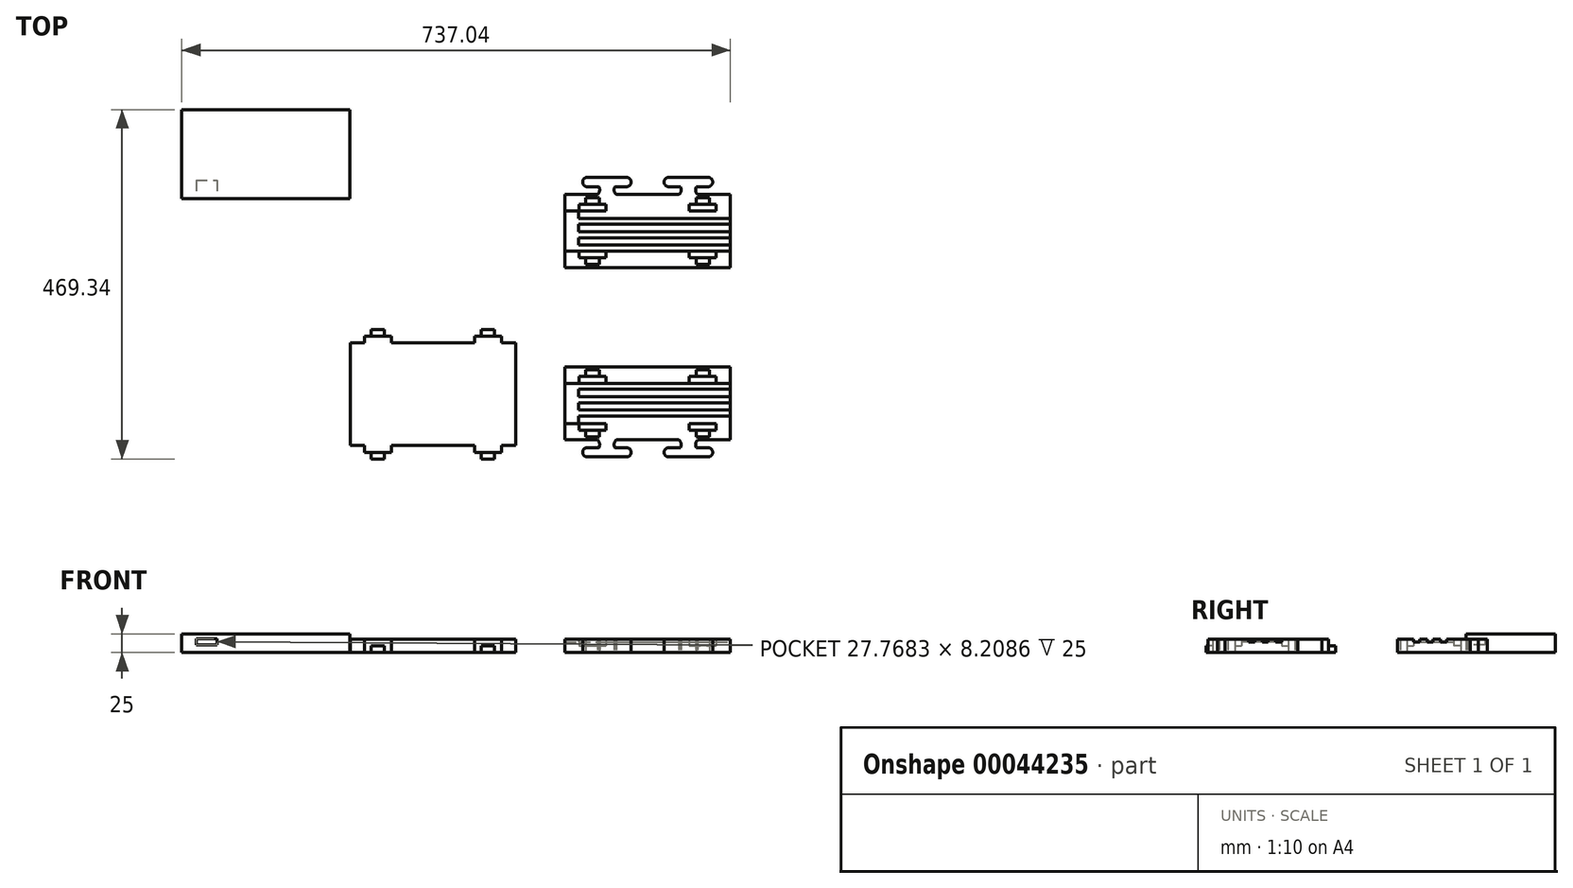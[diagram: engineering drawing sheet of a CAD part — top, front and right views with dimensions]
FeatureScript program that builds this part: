
annotation { "Feature Type Name" : "Feature", "Feature Type Description" : "" }
export const myFeature = defineFeature(function(context is Context, id is Id, definition is map)
    precondition{}
    {
        {
            var Q0;
            Q0=qCreatedBy(makeId("Top.planeOp"),FACE);
            var sketch = newSketch(context, id + "F0", { "sketchPlane" : qUnion([Q0])});
            skLineSegment(sketch, "E0.left", {"start": v(28.08, 92) * mm, "end": v(28.08, -2) * mm});
            skLineSegment(sketch, "E0.right", {"start": v(250.08, 92) * mm, "end": v(250.08, -2) * mm});
            skPoint(sketch, "E1", {"position": v(28.08, 72) * mm});
            skPoint(sketch, "E2", {"position": v(28.08, 18) * mm});
            skPoint(sketch, "E3", {"position": v(28.08, 64) * mm});
            skPoint(sketch, "E4", {"position": v(28.08, 28) * mm});
            skPoint(sketch, "E5", {"position": v(28.08, 54) * mm});
            skPoint(sketch, "E6", {"position": v(29.26, 46) * mm});
            skPoint(sketch, "E7", {"position": v(28.08, 36) * mm});
            skLineSegment(sketch, "E8", {"start": v(28.08, 72) * mm, "end": v(250.08, 72) * mm});
            skLineSegment(sketch, "E9", {"start": v(28.08, 54) * mm, "end": v(250.08, 54) * mm});
            skLineSegment(sketch, "E10", {"start": v(28.08, 36) * mm, "end": v(250.08, 36) * mm});
            skLineSegment(sketch, "E11", {"start": v(28.08, 18) * mm, "end": v(250.08, 18) * mm});
            skPoint(sketch, "E12", {"position": v(102.08, 92) * mm});
            skPoint(sketch, "E13", {"position": v(176.08, 92) * mm});
            skLineSegment(sketch, "E14", {"start": v(102.08, 92) * mm, "end": v(102.08, -2) * mm, "construction": true});
            skLineSegment(sketch, "E15", {"start": v(176.08, 92) * mm, "end": v(176.08, -2) * mm, "construction": true});
            skPoint(sketch, "E16", {"position": v(46.08, 72) * mm});
            skLineSegment(sketch, "E17", {"start": v(46.08, 72) * mm, "end": v(46.08, 18) * mm, "construction": true});
            skPoint(sketch, "E18", {"position": v(46.08, 64) * mm});
            skPoint(sketch, "E19", {"position": v(46.08, 46) * mm});
            skPoint(sketch, "E20", {"position": v(46.08, 28) * mm});
            skLineSegment(sketch, "E21", {"start": v(46.08, 46) * mm, "end": v(250.08, 46) * mm});
            skLineSegment(sketch, "E22", {"start": v(46.08, 64) * mm, "end": v(250.08, 64) * mm});
            skLineSegment(sketch, "E23", {"start": v(46.08, 28) * mm, "end": v(250.08, 28) * mm});
            skPoint(sketch, "E24", {"position": v(213.08, 92) * mm});
            skPoint(sketch, "E25", {"position": v(65.08, 92) * mm});
            skLineSegment(sketch, "E26", {"start": v(65.08, 92) * mm, "end": v(65.08, -2) * mm, "construction": true});
            skLineSegment(sketch, "E27", {"start": v(213.08, 92) * mm, "end": v(213.08, -2) * mm, "construction": true});
            skLineSegment(sketch, "E28", {"start": v(46.08, 64) * mm, "end": v(46.08, 54) * mm});
            skLineSegment(sketch, "E29", {"start": v(46.08, 46) * mm, "end": v(46.08, 36) * mm});
            skLineSegment(sketch, "E30", {"start": v(46.08, 28) * mm, "end": v(46.08, 18) * mm});
            skPoint(sketch, "E31", {"position": v(139.08, 92) * mm});
            skLineSegment(sketch, "E32", {"start": v(139.08, 92) * mm, "end": v(139.08, -2) * mm, "construction": true});
            skLineSegment(sketch, "E33", {"start": v(193.85, -2) * mm, "end": v(193.85, -27) * mm, "construction": true});
            skLineSegment(sketch, "E34", {"start": v(84.31, -2) * mm, "end": v(84.31, -27) * mm, "construction": true});
            skLineSegment(sketch, "E35", {"start": v(84.31, -14.5) * mm, "end": v(193.85, -14.5) * mm, "construction": true});
            skLineSegment(sketch, "E36", {"start": v(84.31, -14.5) * mm, "end": v(31.64, -14.5) * mm, "construction": true});
            skLineSegment(sketch, "E37", {"start": v(193.85, -14.5) * mm, "end": v(246.52, -14.5) * mm, "construction": true});
            skArc(sketch, "E38", {"start": v(206.54, -4) * mm, "mid": v(203.7, -8.9) * mm, "end": v(204.52, -14.5) * mm});
            skArc(sketch, "E39.MirrorCS", {"start": v(97, -4) * mm, "mid": v(94.16, -8.9) * mm, "end": v(94.99, -14.5) * mm});
            skArc(sketch, "E40.MirrorCS", {"start": v(71.63, -4) * mm, "mid": v(74.47, -8.9) * mm, "end": v(73.64, -14.5) * mm});
            skLineSegment(sketch, "E41", {"start": v(73.64, -14.5) * mm, "end": v(57.98, -14.5) * mm});
            skLineSegment(sketch, "E42", {"start": v(94.99, -14.5) * mm, "end": v(110.65, -14.5) * mm});
            skLineSegment(sketch, "E43", {"start": v(183.17, -14.5) * mm, "end": v(167.51, -14.5) * mm});
            skLineSegment(sketch, "E44", {"start": v(204.52, -14.5) * mm, "end": v(220.18, -14.5) * mm});
            skArc(sketch, "E45", {"start": v(57.98, -14.5) * mm, "mid": v(51.73, -20.75) * mm, "end": v(57.98, -27) * mm});
            skArc(sketch, "E46.MirrorCS", {"start": v(110.65, -14.5) * mm, "mid": v(116.9, -20.75) * mm, "end": v(110.65, -27) * mm});
            skArc(sketch, "E47.MirrorCS", {"start": v(167.51, -14.5) * mm, "mid": v(161.26, -20.75) * mm, "end": v(167.51, -27) * mm});
            skArc(sketch, "E48.MirrorCS", {"start": v(220.18, -14.5) * mm, "mid": v(226.43, -20.75) * mm, "end": v(220.18, -27) * mm});
            skLineSegment(sketch, "E49", {"start": v(57.98, -27) * mm, "end": v(110.65, -27) * mm});
            skLineSegment(sketch, "E50", {"start": v(167.51, -27) * mm, "end": v(220.18, -27) * mm});
            skLineSegment(sketch, "E51", {"start": v(-11.33, 160.77) * mm, "end": v(328.55, 160.77) * mm});
            skLineSegment(sketch, "E52.MirrorCS", {"start": v(176.57, 323.54) * mm, "end": v(176.08, 323.54) * mm});
            skPoint(sketch, "E53", {"position": v(65.08, 18) * mm});
            skPoint(sketch, "E54", {"position": v(83.08, 18) * mm});
            skPoint(sketch, "E55", {"position": v(47.08, 18) * mm});
            skPoint(sketch, "E56", {"position": v(65.08, 9) * mm});
            skPoint(sketch, "E57", {"position": v(65.08, 0) * mm});
            skLineSegment(sketch, "E58", {"start": v(47.08, 18) * mm, "end": v(47.08, 9) * mm});
            skLineSegment(sketch, "E59", {"start": v(47.08, 9) * mm, "end": v(65.08, 9) * mm});
            skLineSegment(sketch, "E60", {"start": v(65.08, 9) * mm, "end": v(83.08, 9) * mm});
            skLineSegment(sketch, "E61", {"start": v(83.08, 9) * mm, "end": v(83.08, 18) * mm});
            skLineSegment(sketch, "E62", {"start": v(65.08, 0) * mm, "end": v(74.08, 0) * mm});
            skLineSegment(sketch, "E63", {"start": v(65.08, 0) * mm, "end": v(56.08, 0) * mm});
            skLineSegment(sketch, "E64", {"start": v(74.08, 0) * mm, "end": v(74.08, 9) * mm});
            skLineSegment(sketch, "E65", {"start": v(56.08, 0) * mm, "end": v(56.08, 9) * mm});
            skLineSegment(sketch, "E66.MirrorCS", {"start": v(195.08, 9) * mm, "end": v(195.08, 18) * mm});
            skLineSegment(sketch, "E67.MirrorCS", {"start": v(213.08, 9) * mm, "end": v(195.08, 9) * mm});
            skLineSegment(sketch, "E68.MirrorCS", {"start": v(231.08, 9) * mm, "end": v(213.08, 9) * mm});
            skLineSegment(sketch, "E69.MirrorCS", {"start": v(231.08, 18) * mm, "end": v(231.08, 9) * mm});
            skLineSegment(sketch, "E70.MirrorCS", {"start": v(204.08, 0) * mm, "end": v(204.08, 9) * mm});
            skLineSegment(sketch, "E71.MirrorCS", {"start": v(213.08, 0) * mm, "end": v(204.08, 0) * mm});
            skLineSegment(sketch, "E72.MirrorCS", {"start": v(213.08, 0) * mm, "end": v(222.08, 0) * mm});
            skLineSegment(sketch, "E73.MirrorCS", {"start": v(222.08, 0) * mm, "end": v(222.08, 9) * mm});
            skPoint(sketch, "E74", {"position": v(250.08, 45) * mm});
            skLineSegment(sketch, "E75", {"start": v(250.08, 45) * mm, "end": v(290.41, 45) * mm, "construction": true});
            skLineSegment(sketch, "E76.MirrorCS", {"start": v(195.08, 81) * mm, "end": v(195.08, 72) * mm});
            skLineSegment(sketch, "E77.MirrorCS", {"start": v(231.08, 72) * mm, "end": v(231.08, 81) * mm});
            skLineSegment(sketch, "E78.MirrorCS", {"start": v(231.08, 81) * mm, "end": v(213.08, 81) * mm});
            skLineSegment(sketch, "E79.MirrorCS", {"start": v(213.08, 81) * mm, "end": v(195.08, 81) * mm});
            skLineSegment(sketch, "E80.MirrorCS", {"start": v(204.08, 90) * mm, "end": v(204.08, 81) * mm});
            skLineSegment(sketch, "E81.MirrorCS", {"start": v(213.08, 90) * mm, "end": v(204.08, 90) * mm});
            skLineSegment(sketch, "E82.MirrorCS", {"start": v(213.08, 90) * mm, "end": v(222.08, 90) * mm});
            skLineSegment(sketch, "E83.MirrorCS", {"start": v(222.08, 90) * mm, "end": v(222.08, 81) * mm});
            skLineSegment(sketch, "E84.MirrorCS", {"start": v(83.08, 81) * mm, "end": v(83.08, 72) * mm});
            skLineSegment(sketch, "E85.MirrorCS", {"start": v(65.08, 81) * mm, "end": v(83.08, 81) * mm});
            skLineSegment(sketch, "E86.MirrorCS", {"start": v(47.08, 81) * mm, "end": v(65.08, 81) * mm});
            skLineSegment(sketch, "E87.MirrorCS", {"start": v(47.08, 72) * mm, "end": v(47.08, 81) * mm});
            skLineSegment(sketch, "E88.MirrorCS", {"start": v(56.08, 90) * mm, "end": v(56.08, 81) * mm});
            skLineSegment(sketch, "E89.MirrorCS", {"start": v(65.08, 90) * mm, "end": v(56.08, 90) * mm});
            skLineSegment(sketch, "E90.MirrorCS", {"start": v(65.08, 90) * mm, "end": v(74.08, 90) * mm});
            skLineSegment(sketch, "E91.MirrorCS", {"start": v(74.08, 90) * mm, "end": v(74.08, 81) * mm});
            skLineSegment(sketch, "E92", {"start": v(28.08, 92) * mm, "end": v(28.08, 94) * mm});
            skLineSegment(sketch, "E93", {"start": v(28.08, 94) * mm, "end": v(250.08, 94) * mm});
            skLineSegment(sketch, "E94", {"start": v(250.08, 94) * mm, "end": v(250.08, 92) * mm});
            skLineSegment(sketch, "E95", {"start": v(28.08, -2) * mm, "end": v(28.08, -4) * mm});
            skLineSegment(sketch, "E96", {"start": v(28.08, -4) * mm, "end": v(71.63, -4) * mm});
            skLineSegment(sketch, "E97", {"start": v(97, -4) * mm, "end": v(181.16, -4) * mm});
            skLineSegment(sketch, "E98", {"start": v(206.54, -4) * mm, "end": v(250.08, -4) * mm});
            skLineSegment(sketch, "E99", {"start": v(250.08, -4) * mm, "end": v(250.08, -2) * mm});
            skPoint(sketch, "E100.trimOffspring.start.orphan", {"position": v(211.13, -2) * mm});
            skArc(sketch, "E101.trimOffspring", {"start": v(181.16, -4) * mm, "mid": v(184, -8.9) * mm, "end": v(183.17, -14.5) * mm});
            skPoint(sketch, "E102.MirrorCS.start.orphan", {"position": v(174.62, -2) * mm});
            skPoint(sketch, "E103.start.orphan", {"position": v(176.57, -2) * mm});
            skPoint(sketch, "E104.orphan", {"position": v(158.31, -2) * mm});
            skPoint(sketch, "E105.orphan", {"position": v(119.85, -2) * mm});
            skPoint(sketch, "E106.start.orphan", {"position": v(103.55, -2) * mm});
            skPoint(sketch, "E107.orphan", {"position": v(65.08, -2) * mm});
            skPoint(sketch, "E108.orphan", {"position": v(67.03, -2) * mm});
            skLineSegment(sketch, "E109.MirrorCS", {"start": v(28.08, 227.54) * mm, "end": v(250.08, 227.54) * mm});
            skLineSegment(sketch, "E110.MirrorCS", {"start": v(74.08, 231.54) * mm, "end": v(74.08, 240.54) * mm});
            skLineSegment(sketch, "E111.MirrorCS", {"start": v(65.08, 231.54) * mm, "end": v(74.08, 231.54) * mm});
            skLineSegment(sketch, "E112.MirrorCS", {"start": v(65.08, 231.54) * mm, "end": v(56.08, 231.54) * mm});
            skLineSegment(sketch, "E113.MirrorCS", {"start": v(56.08, 231.54) * mm, "end": v(56.08, 240.54) * mm});
            skLineSegment(sketch, "E114.MirrorCS", {"start": v(65.08, 240.54) * mm, "end": v(83.08, 240.54) * mm});
            skLineSegment(sketch, "E115.MirrorCS", {"start": v(47.08, 240.54) * mm, "end": v(65.08, 240.54) * mm});
            skLineSegment(sketch, "E116.MirrorCS", {"start": v(83.08, 240.54) * mm, "end": v(83.08, 249.54) * mm});
            skLineSegment(sketch, "E117.MirrorCS", {"start": v(47.08, 249.54) * mm, "end": v(47.08, 240.54) * mm});
            skLineSegment(sketch, "E118.MirrorCS", {"start": v(28.08, 249.54) * mm, "end": v(250.08, 249.54) * mm});
            skLineSegment(sketch, "E119.MirrorCS", {"start": v(222.08, 231.54) * mm, "end": v(222.08, 240.54) * mm});
            skLineSegment(sketch, "E120.MirrorCS", {"start": v(213.08, 231.54) * mm, "end": v(222.08, 231.54) * mm});
            skLineSegment(sketch, "E121.MirrorCS", {"start": v(213.08, 231.54) * mm, "end": v(204.08, 231.54) * mm});
            skLineSegment(sketch, "E122.MirrorCS", {"start": v(204.08, 231.54) * mm, "end": v(204.08, 240.54) * mm});
            skLineSegment(sketch, "E123.MirrorCS", {"start": v(213.08, 240.54) * mm, "end": v(195.08, 240.54) * mm});
            skLineSegment(sketch, "E124.MirrorCS", {"start": v(231.08, 240.54) * mm, "end": v(213.08, 240.54) * mm});
            skLineSegment(sketch, "E125.MirrorCS", {"start": v(231.08, 249.54) * mm, "end": v(231.08, 240.54) * mm});
            skLineSegment(sketch, "E126.MirrorCS", {"start": v(195.08, 240.54) * mm, "end": v(195.08, 249.54) * mm});
            skLineSegment(sketch, "E127.MirrorCS", {"start": v(46.08, 257.54) * mm, "end": v(250.08, 257.54) * mm});
            skLineSegment(sketch, "E128.MirrorCS", {"start": v(28.08, 267.54) * mm, "end": v(250.08, 267.54) * mm});
            skLineSegment(sketch, "E129.MirrorCS", {"start": v(46.08, 275.54) * mm, "end": v(250.08, 275.54) * mm});
            skLineSegment(sketch, "E130.MirrorCS", {"start": v(28.08, 285.54) * mm, "end": v(250.08, 285.54) * mm});
            skLineSegment(sketch, "E131.MirrorCS", {"start": v(46.08, 293.54) * mm, "end": v(250.08, 293.54) * mm});
            skLineSegment(sketch, "E132.MirrorCS", {"start": v(28.08, 303.54) * mm, "end": v(250.08, 303.54) * mm});
            skLineSegment(sketch, "E133.MirrorCS", {"start": v(250.08, 229.54) * mm, "end": v(250.08, 323.54) * mm});
            skLineSegment(sketch, "E134.MirrorCS", {"start": v(250.08, 227.54) * mm, "end": v(250.08, 229.54) * mm});
            skLineSegment(sketch, "E135.MirrorCS", {"start": v(28.08, 229.54) * mm, "end": v(28.08, 227.54) * mm});
            skLineSegment(sketch, "E136.MirrorCS", {"start": v(28.08, 229.54) * mm, "end": v(28.08, 323.54) * mm});
            skLineSegment(sketch, "E137.MirrorCS", {"start": v(28.08, 323.54) * mm, "end": v(28.08, 325.54) * mm});
            skLineSegment(sketch, "E138.MirrorCS", {"start": v(250.08, 325.54) * mm, "end": v(250.08, 323.54) * mm});
            skLineSegment(sketch, "E139.MirrorCS", {"start": v(206.54, 325.54) * mm, "end": v(250.08, 325.54) * mm});
            skArc(sketch, "E140.MirrorCS", {"start": v(206.54, 325.54) * mm, "mid": v(203.7, 330.44) * mm, "end": v(204.52, 336.04) * mm});
            skLineSegment(sketch, "E141.MirrorCS", {"start": v(204.52, 336.04) * mm, "end": v(220.18, 336.04) * mm});
            skArc(sketch, "E142.MirrorCS", {"start": v(220.18, 336.04) * mm, "mid": v(226.43, 342.29) * mm, "end": v(220.18, 348.54) * mm});
            skLineSegment(sketch, "E143.MirrorCS", {"start": v(167.51, 348.54) * mm, "end": v(220.18, 348.54) * mm});
            skArc(sketch, "E144.MirrorCS", {"start": v(167.51, 336.04) * mm, "mid": v(161.26, 342.29) * mm, "end": v(167.51, 348.54) * mm});
            skLineSegment(sketch, "E145.MirrorCS", {"start": v(183.17, 336.04) * mm, "end": v(167.51, 336.04) * mm});
            skArc(sketch, "E146.MirrorCS", {"start": v(181.16, 325.54) * mm, "mid": v(184, 330.44) * mm, "end": v(183.17, 336.04) * mm});
            skLineSegment(sketch, "E147.MirrorCS", {"start": v(97, 325.54) * mm, "end": v(181.16, 325.54) * mm});
            skArc(sketch, "E148.MirrorCS", {"start": v(97, 325.54) * mm, "mid": v(94.16, 330.44) * mm, "end": v(94.99, 336.04) * mm});
            skLineSegment(sketch, "E149.MirrorCS", {"start": v(94.99, 336.04) * mm, "end": v(110.65, 336.04) * mm});
            skArc(sketch, "E150.MirrorCS", {"start": v(110.65, 336.04) * mm, "mid": v(116.9, 342.29) * mm, "end": v(110.65, 348.54) * mm});
            skLineSegment(sketch, "E151.MirrorCS", {"start": v(57.98, 348.54) * mm, "end": v(110.65, 348.54) * mm});
            skArc(sketch, "E152.MirrorCS", {"start": v(57.98, 336.04) * mm, "mid": v(51.73, 342.29) * mm, "end": v(57.98, 348.54) * mm});
            skLineSegment(sketch, "E153.MirrorCS", {"start": v(73.64, 336.04) * mm, "end": v(57.98, 336.04) * mm});
            skArc(sketch, "E154.MirrorCS", {"start": v(71.63, 325.54) * mm, "mid": v(74.47, 330.44) * mm, "end": v(73.64, 336.04) * mm});
            skLineSegment(sketch, "E155.MirrorCS", {"start": v(28.08, 325.54) * mm, "end": v(71.63, 325.54) * mm});
            skLineSegment(sketch, "E156.MirrorCS", {"start": v(83.08, 312.54) * mm, "end": v(83.08, 303.54) * mm});
            skLineSegment(sketch, "E157.MirrorCS", {"start": v(65.08, 312.54) * mm, "end": v(83.08, 312.54) * mm});
            skLineSegment(sketch, "E158.MirrorCS", {"start": v(47.08, 312.54) * mm, "end": v(65.08, 312.54) * mm});
            skLineSegment(sketch, "E159.MirrorCS", {"start": v(47.08, 303.54) * mm, "end": v(47.08, 312.54) * mm});
            skLineSegment(sketch, "E160.MirrorCS", {"start": v(56.08, 321.54) * mm, "end": v(56.08, 312.54) * mm});
            skLineSegment(sketch, "E161.MirrorCS", {"start": v(65.08, 321.54) * mm, "end": v(56.08, 321.54) * mm});
            skLineSegment(sketch, "E162.MirrorCS", {"start": v(65.08, 321.54) * mm, "end": v(74.08, 321.54) * mm});
            skLineSegment(sketch, "E163.MirrorCS", {"start": v(74.08, 321.54) * mm, "end": v(74.08, 312.54) * mm});
            skLineSegment(sketch, "E164.MirrorCS", {"start": v(195.08, 312.54) * mm, "end": v(195.08, 303.54) * mm});
            skLineSegment(sketch, "E165.MirrorCS", {"start": v(213.08, 312.54) * mm, "end": v(195.08, 312.54) * mm});
            skLineSegment(sketch, "E166.MirrorCS", {"start": v(231.08, 312.54) * mm, "end": v(213.08, 312.54) * mm});
            skLineSegment(sketch, "E167.MirrorCS", {"start": v(231.08, 303.54) * mm, "end": v(231.08, 312.54) * mm});
            skLineSegment(sketch, "E168.MirrorCS", {"start": v(222.08, 321.54) * mm, "end": v(222.08, 312.54) * mm});
            skLineSegment(sketch, "E169.MirrorCS", {"start": v(213.08, 321.54) * mm, "end": v(222.08, 321.54) * mm});
            skLineSegment(sketch, "E170.MirrorCS", {"start": v(213.08, 321.54) * mm, "end": v(204.08, 321.54) * mm});
            skLineSegment(sketch, "E171.MirrorCS", {"start": v(204.08, 321.54) * mm, "end": v(204.08, 312.54) * mm});
            skLineSegment(sketch, "E172.MirrorCS", {"start": v(46.08, 257.54) * mm, "end": v(46.08, 267.54) * mm});
            skLineSegment(sketch, "E173.MirrorCS", {"start": v(46.08, 275.54) * mm, "end": v(46.08, 285.54) * mm});
            skLineSegment(sketch, "E174.MirrorCS", {"start": v(46.08, 293.54) * mm, "end": v(46.08, 303.54) * mm});
            skSolve(sketch);
        }
        {
            var Q0;
            Q0=qCreatedBy(makeId("Top.planeOp"),FACE);
            var sketch = newSketch(context, id + "F1", { "sketchPlane" : qUnion([Q0])});
            skLineSegment(sketch, "E175.bottom", {"start": v(-260.45, 126.28) * mm, "end": v(-186.45, 126.28) * mm});
            skLineSegment(sketch, "E175.top", {"start": v(-260.45, -11.72) * mm, "end": v(-38.45, -11.72) * mm});
            skLineSegment(sketch, "E175.left", {"start": v(-260.45, 126.28) * mm, "end": v(-260.45, -11.72) * mm});
            skLineSegment(sketch, "E175.right", {"start": v(-38.45, 126.28) * mm, "end": v(-38.45, -11.72) * mm});
            skPoint(sketch, "E176", {"position": v(-186.45, 126.28) * mm});
            skPoint(sketch, "E177", {"position": v(-112.45, 126.28) * mm});
            skLineSegment(sketch, "E178", {"start": v(-260.45, 57.28) * mm, "end": v(-38.45, 57.28) * mm, "construction": true});
            skLineSegment(sketch, "E179", {"start": v(-186.45, 126.28) * mm, "end": v(-186.45, -11.72) * mm, "construction": true});
            skLineSegment(sketch, "E180", {"start": v(-112.45, 126.28) * mm, "end": v(-112.45, -11.72) * mm, "construction": true});
            skLineSegment(sketch, "E181.trimOffspring", {"start": v(-112.45, 126.28) * mm, "end": v(-75.45, 126.28) * mm});
            skLineSegment(sketch, "E182", {"start": v(-112.45, 126.28) * mm, "end": v(-186.45, 126.28) * mm});
            skLineSegment(sketch, "E183", {"start": v(-149.45, 126.28) * mm, "end": v(-149.45, -11.72) * mm, "construction": true});
            skLineSegment(sketch, "E184", {"start": v(-223.45, 126.28) * mm, "end": v(-223.45, -11.72) * mm, "construction": true});
            skLineSegment(sketch, "E185", {"start": v(-75.45, 126.28) * mm, "end": v(-75.45, -11.72) * mm, "construction": true});
            skPoint(sketch, "E186", {"position": v(-57.45, 126.28) * mm});
            skLineSegment(sketch, "E187", {"start": v(-57.45, 126.28) * mm, "end": v(-57.45, 135.28) * mm});
            skLineSegment(sketch, "E188", {"start": v(-66.45, 144.28) * mm, "end": v(-75.45, 144.28) * mm});
            skLineSegment(sketch, "E189.trimOffspring", {"start": v(-57.45, 126.28) * mm, "end": v(-38.45, 126.28) * mm});
            skLineSegment(sketch, "E190", {"start": v(-57.45, 126.28) * mm, "end": v(-75.45, 126.28) * mm});
            skLineSegment(sketch, "E191", {"start": v(-66.45, 126.28) * mm, "end": v(-66.45, 135.28) * mm});
            skPoint(sketch, "E191.endSnap0", {"position": v(-57.45, 135.28) * mm});
            skLineSegment(sketch, "E192", {"start": v(-66.45, 135.28) * mm, "end": v(-75.45, 135.28) * mm});
            skLineSegment(sketch, "E193.MirrorCS", {"start": v(-66.45, -20.72) * mm, "end": v(-75.45, -20.72) * mm});
            skLineSegment(sketch, "E194.MirrorCS", {"start": v(-66.45, -29.72) * mm, "end": v(-75.45, -29.72) * mm});
            skLineSegment(sketch, "E195.MirrorCS", {"start": v(-57.45, -11.72) * mm, "end": v(-57.45, -20.72) * mm});
            skLineSegment(sketch, "E196.MirrorCS", {"start": v(-66.45, -11.72) * mm, "end": v(-66.45, -20.72) * mm});
            skLineSegment(sketch, "E197.MirrorCS", {"start": v(-232.45, 135.28) * mm, "end": v(-223.45, 135.28) * mm});
            skLineSegment(sketch, "E198.MirrorCS", {"start": v(-232.45, 144.28) * mm, "end": v(-223.45, 144.28) * mm});
            skLineSegment(sketch, "E199.MirrorCS", {"start": v(-241.45, 126.28) * mm, "end": v(-241.45, 135.28) * mm});
            skLineSegment(sketch, "E200.MirrorCS", {"start": v(-232.45, 126.28) * mm, "end": v(-232.45, 135.28) * mm});
            skLineSegment(sketch, "E201.MirrorCS", {"start": v(-232.45, -11.72) * mm, "end": v(-232.45, -20.72) * mm});
            skLineSegment(sketch, "E202.MirrorCS", {"start": v(-232.45, -20.72) * mm, "end": v(-223.45, -20.72) * mm});
            skLineSegment(sketch, "E203.MirrorCS", {"start": v(-232.45, -29.72) * mm, "end": v(-223.45, -29.72) * mm});
            skLineSegment(sketch, "E204.MirrorCS", {"start": v(-241.45, -11.72) * mm, "end": v(-241.45, -20.72) * mm});
            skLineSegment(sketch, "E205.MirrorCS", {"start": v(-84.45, 135.28) * mm, "end": v(-75.45, 135.28) * mm});
            skLineSegment(sketch, "E206.MirrorCS", {"start": v(-84.45, 126.28) * mm, "end": v(-84.45, 135.28) * mm});
            skLineSegment(sketch, "E207.MirrorCS", {"start": v(-93.45, 126.28) * mm, "end": v(-93.45, 135.28) * mm});
            skLineSegment(sketch, "E208.MirrorCS", {"start": v(-84.45, 144.28) * mm, "end": v(-75.45, 144.28) * mm});
            skLineSegment(sketch, "E209.MirrorCS", {"start": v(-84.45, -11.72) * mm, "end": v(-84.45, -20.72) * mm});
            skLineSegment(sketch, "E210.MirrorCS", {"start": v(-84.45, -20.72) * mm, "end": v(-75.45, -20.72) * mm});
            skLineSegment(sketch, "E211.MirrorCS", {"start": v(-84.45, -29.72) * mm, "end": v(-75.45, -29.72) * mm});
            skLineSegment(sketch, "E212.MirrorCS", {"start": v(-93.45, -11.72) * mm, "end": v(-93.45, -20.72) * mm});
            skLineSegment(sketch, "E213.MirrorCS", {"start": v(-214.45, 126.28) * mm, "end": v(-214.45, 135.28) * mm});
            skLineSegment(sketch, "E214.MirrorCS", {"start": v(-214.45, 135.28) * mm, "end": v(-223.45, 135.28) * mm});
            skLineSegment(sketch, "E215.MirrorCS", {"start": v(-214.45, 144.28) * mm, "end": v(-223.45, 144.28) * mm});
            skLineSegment(sketch, "E216.MirrorCS", {"start": v(-205.45, 126.28) * mm, "end": v(-205.45, 135.28) * mm});
            skLineSegment(sketch, "E217.MirrorCS", {"start": v(-205.45, -11.72) * mm, "end": v(-205.45, -20.72) * mm});
            skLineSegment(sketch, "E218.MirrorCS", {"start": v(-214.45, -11.72) * mm, "end": v(-214.45, -20.72) * mm});
            skLineSegment(sketch, "E219.MirrorCS", {"start": v(-214.45, -20.72) * mm, "end": v(-223.45, -20.72) * mm});
            skLineSegment(sketch, "E220.MirrorCS", {"start": v(-214.45, -29.72) * mm, "end": v(-223.45, -29.72) * mm});
            skLineSegment(sketch, "E221", {"start": v(-84.45, 135.28) * mm, "end": v(-84.45, 144.28) * mm});
            skLineSegment(sketch, "E222", {"start": v(-66.45, 135.28) * mm, "end": v(-66.45, 144.28) * mm});
            skLineSegment(sketch, "E223", {"start": v(-66.45, 135.28) * mm, "end": v(-57.45, 135.28) * mm});
            skLineSegment(sketch, "E224", {"start": v(-84.45, 135.28) * mm, "end": v(-93.45, 135.28) * mm});
            skPoint(sketch, "E225.orphan", {"position": v(-93.45, 144.28) * mm});
            skPoint(sketch, "E226.orphan", {"position": v(-57.45, 144.28) * mm});
            skLineSegment(sketch, "E227", {"start": v(-66.45, -20.72) * mm, "end": v(-66.45, -29.72) * mm});
            skLineSegment(sketch, "E228", {"start": v(-84.45, -20.72) * mm, "end": v(-84.45, -29.72) * mm});
            skLineSegment(sketch, "E229", {"start": v(-84.45, -20.72) * mm, "end": v(-93.45, -20.72) * mm});
            skLineSegment(sketch, "E230", {"start": v(-66.45, -20.72) * mm, "end": v(-57.45, -20.72) * mm});
            skPoint(sketch, "E231.orphan", {"position": v(-57.45, -29.72) * mm});
            skPoint(sketch, "E232.orphan", {"position": v(-93.45, -29.72) * mm});
            skLineSegment(sketch, "E233", {"start": v(-214.45, -20.72) * mm, "end": v(-205.45, -20.72) * mm});
            skLineSegment(sketch, "E234", {"start": v(-232.45, -20.72) * mm, "end": v(-241.45, -20.72) * mm});
            skLineSegment(sketch, "E235", {"start": v(-232.45, -20.72) * mm, "end": v(-232.45, -29.72) * mm});
            skLineSegment(sketch, "E236", {"start": v(-214.45, -20.72) * mm, "end": v(-214.45, -29.72) * mm});
            skPoint(sketch, "E237.orphan", {"position": v(-205.45, -29.72) * mm});
            skPoint(sketch, "E238.orphan", {"position": v(-241.45, -29.72) * mm});
            skLineSegment(sketch, "E239", {"start": v(-214.45, 135.28) * mm, "end": v(-205.45, 135.28) * mm});
            skLineSegment(sketch, "E240", {"start": v(-232.45, 135.28) * mm, "end": v(-241.45, 135.28) * mm});
            skLineSegment(sketch, "E241", {"start": v(-232.45, 135.28) * mm, "end": v(-232.45, 144.28) * mm});
            skLineSegment(sketch, "E242", {"start": v(-214.45, 135.28) * mm, "end": v(-214.45, 144.28) * mm});
            skPoint(sketch, "E243.orphan", {"position": v(-205.45, 144.28) * mm});
            skPoint(sketch, "E244.orphan", {"position": v(-241.45, 144.28) * mm});
            skSolve(sketch);
        }
        {
            var Q0;
            {var subQ1=sQuery(id+"F1.wireOp",EDGE,"E175.left");Q0=makeQuery(id+"F1.imprint","IMPRINT",FACE,{"disambiguationData":[TD([[makeQuery(id+"F1.imprint","IMPRINT",EDGE,{"derivedFrom":subQ1}),1.0]])]});}
            var Q1;
            {var subQ1=sQuery(id+"F1.wireOp",EDGE,"E201.MirrorCS");Q1=makeQuery(id+"F1.imprint","IMPRINT",FACE,{"disambiguationData":[TD([[makeQuery(id+"F1.imprint","IMPRINT",EDGE,{"derivedFrom":subQ1}),1.0]])]});}
            var Q2;
            Q2=makeQuery(id+"F1.imprint","IMPRINT",FACE,{"disambiguationData":[TD([[makeQuery(id+"F1.imprint","IMPRINT",EDGE,{"derivedFrom":sQuery(id+"F1.wireOp",EDGE,"E193.MirrorCS")}),-1.0]])]});
            var Q3;
            {var subQ0=sQuery(id+"F1.wireOp",EDGE,"E191");Q3=makeQuery(id+"F1.imprint","IMPRINT",FACE,{"disambiguationData":[TD([[makeQuery(id+"F1.imprint","IMPRINT",EDGE,{"derivedFrom":subQ0}),1.0]])]});}
            var Q4;
            Q4=makeQuery(id+"F1.imprint","IMPRINT",FACE,{"disambiguationData":[TD([[makeQuery(id+"F1.imprint","IMPRINT",EDGE,{"derivedFrom":sQuery(id+"F1.wireOp",EDGE,"E197.MirrorCS")}),-1.0]])]});
            var Q5;
            {var subQ0=sQuery(id+"F1.wireOp",EDGE,"E217.MirrorCS");Q5=makeQuery(id+"F1.imprint","IMPRINT",FACE,{"disambiguationData":[TD([[makeQuery(id+"F1.imprint","IMPRINT",EDGE,{"derivedFrom":subQ0}),-1.0]])]});}
            var Q6;
            {var subQ0=sQuery(id+"F1.wireOp",EDGE,"E201.MirrorCS");Q6=makeQuery(id+"F1.imprint","IMPRINT",FACE,{"disambiguationData":[TD([[makeQuery(id+"F1.imprint","IMPRINT",EDGE,{"derivedFrom":subQ0}),-1.0]])]});}
            var Q7;
            {var subQ0=sQuery(id+"F1.wireOp",EDGE,"E209.MirrorCS");Q7=makeQuery(id+"F1.imprint","IMPRINT",FACE,{"disambiguationData":[TD([[makeQuery(id+"F1.imprint","IMPRINT",EDGE,{"derivedFrom":subQ0}),-1.0]])]});}
            var Q8;
            {var subQ0=sQuery(id+"F1.wireOp",EDGE,"E195.MirrorCS");Q8=makeQuery(id+"F1.imprint","IMPRINT",FACE,{"disambiguationData":[TD([[makeQuery(id+"F1.imprint","IMPRINT",EDGE,{"derivedFrom":subQ0}),-1.0]])]});}
            var Q9;
            {var subQ0=sQuery(id+"F1.wireOp",EDGE,"E187");Q9=makeQuery(id+"F1.imprint","IMPRINT",FACE,{"disambiguationData":[TD([[makeQuery(id+"F1.imprint","IMPRINT",EDGE,{"derivedFrom":subQ0}),1.0]])]});}
            var Q10;
            {var subQ0=sQuery(id+"F1.wireOp",EDGE,"E206.MirrorCS");Q10=makeQuery(id+"F1.imprint","IMPRINT",FACE,{"disambiguationData":[TD([[makeQuery(id+"F1.imprint","IMPRINT",EDGE,{"derivedFrom":subQ0}),1.0]])]});}
            var Q11;
            {var subQ0=sQuery(id+"F1.wireOp",EDGE,"E213.MirrorCS");Q11=makeQuery(id+"F1.imprint","IMPRINT",FACE,{"disambiguationData":[TD([[makeQuery(id+"F1.imprint","IMPRINT",EDGE,{"derivedFrom":subQ0}),-1.0]])]});}
            var Q12;
            {var subQ0=sQuery(id+"F1.wireOp",EDGE,"E199.MirrorCS");Q12=makeQuery(id+"F1.imprint","IMPRINT",FACE,{"disambiguationData":[TD([[makeQuery(id+"F1.imprint","IMPRINT",EDGE,{"derivedFrom":subQ0}),-1.0]])]});}
            extrude(context, id + "F2", {"entities" : qUnion([Q0, Q1, Q2, Q3, Q4, Q5, Q6, Q7, Q8, Q9, Q10, Q11, Q12]), "depth" : 18 * mm});
        }
        {
            var Q0;
            Q0=makeQuery(id+"F1.imprint","IMPRINT",FACE,{"disambiguationData":[TD([[makeQuery(id+"F1.imprint","IMPRINT",EDGE,{"derivedFrom":sQuery(id+"F1.wireOp",EDGE,"E202.MirrorCS")}),-1.0]])]});
            var Q1;
            Q1=makeQuery(id+"F1.imprint","IMPRINT",FACE,{"disambiguationData":[TD([[makeQuery(id+"F1.imprint","IMPRINT",EDGE,{"derivedFrom":sQuery(id+"F1.wireOp",EDGE,"E193.MirrorCS")}),1.0]])]});
            var Q2;
            Q2=makeQuery(id+"F1.imprint","IMPRINT",FACE,{"disambiguationData":[TD([[makeQuery(id+"F1.imprint","IMPRINT",EDGE,{"derivedFrom":sQuery(id+"F1.wireOp",EDGE,"E188")}),1.0]])]});
            var Q3;
            Q3=makeQuery(id+"F1.imprint","IMPRINT",FACE,{"disambiguationData":[TD([[makeQuery(id+"F1.imprint","IMPRINT",EDGE,{"derivedFrom":sQuery(id+"F1.wireOp",EDGE,"E197.MirrorCS")}),1.0]])]});
            extrude(context, id + "F3", {"entities" : qUnion([Q0, Q1, Q2, Q3]), "operationType" : NewBodyOperationType.ADD, "depth" : 9 * mm});
        }
        {
            var Q0;
            {var subQ5=sQuery(id+"F0.wireOp",EDGE,"E76.MirrorCS");Q0=makeQuery(id+"F0.imprint","IMPRINT",FACE,{"disambiguationData":[TD([[makeQuery(id+"F0.imprint","IMPRINT",EDGE,{"derivedFrom":subQ5}),-1.0]])]});}
            var Q1;
            {var subQ3=sQuery(id+"F0.wireOp",EDGE,"E22");Q1=makeQuery(id+"F0.imprint","IMPRINT",FACE,{"disambiguationData":[TD([[makeQuery(id+"F0.imprint","IMPRINT",EDGE,{"derivedFrom":subQ3}),-1.0]])]});}
            var Q2;
            {var subQ3=sQuery(id+"F0.wireOp",EDGE,"E21");Q2=makeQuery(id+"F0.imprint","IMPRINT",FACE,{"disambiguationData":[TD([[makeQuery(id+"F0.imprint","IMPRINT",EDGE,{"derivedFrom":subQ3}),-1.0]])]});}
            var Q3;
            {var subQ7=sQuery(id+"F0.wireOp",EDGE,"E23");Q3=makeQuery(id+"F0.imprint","IMPRINT",FACE,{"disambiguationData":[TD([[makeQuery(id+"F0.imprint","IMPRINT",EDGE,{"derivedFrom":subQ7}),-1.0]])]});}
            var Q4;
            Q4=makeQuery(id+"F0.imprint","IMPRINT",FACE,{"disambiguationData":[TD([[makeQuery(id+"F0.imprint","IMPRINT",EDGE,{"derivedFrom":sQuery(id+"F0.wireOp",EDGE,"E38")}),-1.0]])]});
            var Q5;
            Q5=makeQuery(id+"F0.imprint","IMPRINT",FACE,{"disambiguationData":[TD([[makeQuery(id+"F0.imprint","IMPRINT",EDGE,{"derivedFrom":sQuery(id+"F0.wireOp",EDGE,"E109.MirrorCS")}),1.0]])]});
            var Q6;
            {var subQ0=sQuery(id+"F0.wireOp",EDGE,"E127.MirrorCS");Q6=makeQuery(id+"F0.imprint","IMPRINT",FACE,{"disambiguationData":[TD([[makeQuery(id+"F0.imprint","IMPRINT",EDGE,{"derivedFrom":subQ0}),1.0]])]});}
            var Q7;
            {var subQ0=sQuery(id+"F0.wireOp",EDGE,"E129.MirrorCS");Q7=makeQuery(id+"F0.imprint","IMPRINT",FACE,{"disambiguationData":[TD([[makeQuery(id+"F0.imprint","IMPRINT",EDGE,{"derivedFrom":subQ0}),1.0]])]});}
            var Q8;
            {var subQ5=sQuery(id+"F0.wireOp",EDGE,"E131.MirrorCS");Q8=makeQuery(id+"F0.imprint","IMPRINT",FACE,{"disambiguationData":[TD([[makeQuery(id+"F0.imprint","IMPRINT",EDGE,{"derivedFrom":subQ5}),1.0]])]});}
            var Q9;
            {var subQ4=sQuery(id+"F0.wireOp",EDGE,"E137.MirrorCS");Q9=makeQuery(id+"F0.imprint","IMPRINT",FACE,{"disambiguationData":[TD([[makeQuery(id+"F0.imprint","IMPRINT",EDGE,{"derivedFrom":subQ4}),-1.0]])]});}
            extrude(context, id + "F4", {"entities" : qUnion([Q0, Q1, Q2, Q3, Q4, Q5, Q6, Q7, Q8, Q9]), "depth" : 18 * mm});
        }
        {
            var Q0;
            {var subQ6=sQuery(id+"F0.wireOp",EDGE,"E23");Q0=makeQuery(id+"F0.imprint","IMPRINT",FACE,{"disambiguationData":[TD([[makeQuery(id+"F0.imprint","IMPRINT",EDGE,{"derivedFrom":subQ6}),1.0]])]});}
            var Q1;
            {var subQ4=sQuery(id+"F0.wireOp",EDGE,"E21");Q1=makeQuery(id+"F0.imprint","IMPRINT",FACE,{"disambiguationData":[TD([[makeQuery(id+"F0.imprint","IMPRINT",EDGE,{"derivedFrom":subQ4}),1.0]])]});}
            var Q2;
            {var subQ10=sQuery(id+"F0.wireOp",EDGE,"E22");Q2=makeQuery(id+"F0.imprint","IMPRINT",FACE,{"disambiguationData":[TD([[makeQuery(id+"F0.imprint","IMPRINT",EDGE,{"derivedFrom":subQ10}),1.0]])]});}
            var Q3;
            {var subQ11=sQuery(id+"F0.wireOp",EDGE,"E127.MirrorCS");Q3=makeQuery(id+"F0.imprint","IMPRINT",FACE,{"disambiguationData":[TD([[makeQuery(id+"F0.imprint","IMPRINT",EDGE,{"derivedFrom":subQ11}),-1.0]])]});}
            var Q4;
            {var subQ4=sQuery(id+"F0.wireOp",EDGE,"E129.MirrorCS");Q4=makeQuery(id+"F0.imprint","IMPRINT",FACE,{"disambiguationData":[TD([[makeQuery(id+"F0.imprint","IMPRINT",EDGE,{"derivedFrom":subQ4}),-1.0]])]});}
            var Q5;
            {var subQ4=sQuery(id+"F0.wireOp",EDGE,"E131.MirrorCS");Q5=makeQuery(id+"F0.imprint","IMPRINT",FACE,{"disambiguationData":[TD([[makeQuery(id+"F0.imprint","IMPRINT",EDGE,{"derivedFrom":subQ4}),-1.0]])]});}
            extrude(context, id + "F5", {"entities" : qUnion([Q0, Q1, Q2, Q3, Q4, Q5]), "operationType" : NewBodyOperationType.ADD, "depth" : 14 * mm});
        }
        {
            var Q0;
            Q0=qCreatedBy(makeId("Top.planeOp"),FACE);
            var sketch = newSketch(context, id + "F6", { "sketchPlane" : qUnion([Q0])});
            skLineSegment(sketch, "E245.bottom", {"start": v(-486.96, 439.62) * mm, "end": v(-261, 439.62) * mm});
            skLineSegment(sketch, "E245.top", {"start": v(-486.96, 319.91) * mm, "end": v(-261, 319.91) * mm});
            skLineSegment(sketch, "E245.left", {"start": v(-486.96, 439.62) * mm, "end": v(-486.96, 319.91) * mm});
            skLineSegment(sketch, "E245.right", {"start": v(-261, 439.62) * mm, "end": v(-261, 319.91) * mm});
            skSolve(sketch);
        }
        {
            var Q0;
            Q0=makeQuery(id+"F6.imprint","IMPRINT",FACE,{"disambiguationData":[TD([[makeQuery(id+"F6.imprint","IMPRINT",EDGE,{"derivedFrom":sQuery(id+"F6.wireOp",EDGE,"E245.bottom")}),-1.0]])]});
            extrude(context, id + "F7", {"entities" : qUnion([Q0]), "depth" : 25 * mm});
        }
        {
            var Q0;
            Q0=makeQuery(id+"F7.opExtrude","SWEPT_FACE",FACE,{"disambiguationData":[OSD([sQuery(id+"F6.wireOp",EDGE,"E245.top")])]});
            var sketch = newSketch(context, id + "F8", { "sketchPlane" : qUnion([Q0])});
            skLineSegment(sketch, "E246.bottom", {"start": v(-467.55, 18.6) * mm, "end": v(-439.78, 18.6) * mm});
            skLineSegment(sketch, "E246.top", {"start": v(-467.55, 10.4) * mm, "end": v(-439.78, 10.4) * mm});
            skLineSegment(sketch, "E246.left", {"start": v(-467.55, 18.6) * mm, "end": v(-467.55, 10.4) * mm});
            skLineSegment(sketch, "E246.right", {"start": v(-439.78, 18.6) * mm, "end": v(-439.78, 10.4) * mm});
            skLineSegment(sketch, "E247.bottom", {"start": v(-390.98, 25) * mm, "end": v(-373.98, 25) * mm});
            skLineSegment(sketch, "E247.top", {"start": v(-390.98, 0) * mm, "end": v(-373.98, 0) * mm});
            skLineSegment(sketch, "E247.left", {"start": v(-390.98, 25) * mm, "end": v(-390.98, 0) * mm});
            skLineSegment(sketch, "E247.right", {"start": v(-373.98, 25) * mm, "end": v(-373.98, 0) * mm});
            skLineSegment(sketch, "E248.bottom", {"start": v(-332.74, 17.4) * mm, "end": v(-314.13, 17.4) * mm});
            skLineSegment(sketch, "E248.top", {"start": v(-332.74, 4.95) * mm, "end": v(-314.13, 4.95) * mm});
            skLineSegment(sketch, "E248.left", {"start": v(-332.74, 17.4) * mm, "end": v(-332.74, 4.95) * mm});
            skLineSegment(sketch, "E248.right", {"start": v(-314.13, 17.4) * mm, "end": v(-314.13, 4.95) * mm});
            skSolve(sketch);
        }
        {
            var Q0;
            Q0=makeQuery(id+"F8.imprint","IMPRINT",FACE,{"disambiguationData":[TD([[makeQuery(id+"F8.imprint","IMPRINT",EDGE,{"derivedFrom":sQuery(id+"F8.wireOp",EDGE,"E246.bottom")}),-1.0]])]});
            extrude(context, id + "F9", {"entities" : qUnion([Q0]), "operationType" : NewBodyOperationType.REMOVE, "oppositeDirection" : true, "depth" : 25 * mm});
        }
        {
            var Q0;
            {var subQ1=sQuery(id+"F0.wireOp",EDGE,"E156.MirrorCS");Q0=makeQuery(id+"F0.imprint","IMPRINT",FACE,{"disambiguationData":[TD([[makeQuery(id+"F0.imprint","IMPRINT",EDGE,{"derivedFrom":subQ1}),-1.0]])]});}
            var Q1;
            {var subQ1=sQuery(id+"F0.wireOp",EDGE,"E164.MirrorCS");Q1=makeQuery(id+"F0.imprint","IMPRINT",FACE,{"disambiguationData":[TD([[makeQuery(id+"F0.imprint","IMPRINT",EDGE,{"derivedFrom":subQ1}),1.0]])]});}
            var Q2;
            {var subQ2=sQuery(id+"F0.wireOp",EDGE,"E125.MirrorCS");Q2=makeQuery(id+"F0.imprint","IMPRINT",FACE,{"disambiguationData":[TD([[makeQuery(id+"F0.imprint","IMPRINT",EDGE,{"derivedFrom":subQ2}),-1.0]])]});}
            var Q3;
            {var subQ6=sQuery(id+"F0.wireOp",EDGE,"E116.MirrorCS");Q3=makeQuery(id+"F0.imprint","IMPRINT",FACE,{"disambiguationData":[TD([[makeQuery(id+"F0.imprint","IMPRINT",EDGE,{"derivedFrom":subQ6}),1.0]])]});}
            var Q4;
            {var subQ1=sQuery(id+"F0.wireOp",EDGE,"E84.MirrorCS");Q4=makeQuery(id+"F0.imprint","IMPRINT",FACE,{"disambiguationData":[TD([[makeQuery(id+"F0.imprint","IMPRINT",EDGE,{"derivedFrom":subQ1}),-1.0]])]});}
            var Q5;
            {var subQ0=sQuery(id+"F0.wireOp",EDGE,"E76.MirrorCS");Q5=makeQuery(id+"F0.imprint","IMPRINT",FACE,{"disambiguationData":[TD([[makeQuery(id+"F0.imprint","IMPRINT",EDGE,{"derivedFrom":subQ0}),1.0]])]});}
            var Q6;
            {var subQ1=sQuery(id+"F0.wireOp",EDGE,"E66.MirrorCS");Q6=makeQuery(id+"F0.imprint","IMPRINT",FACE,{"disambiguationData":[TD([[makeQuery(id+"F0.imprint","IMPRINT",EDGE,{"derivedFrom":subQ1}),-1.0]])]});}
            var Q7;
            {var subQ4=sQuery(id+"F0.wireOp",EDGE,"E58");Q7=makeQuery(id+"F0.imprint","IMPRINT",FACE,{"disambiguationData":[TD([[makeQuery(id+"F0.imprint","IMPRINT",EDGE,{"derivedFrom":subQ4}),1.0]])]});}
            extrude(context, id + "F10", {"entities" : qUnion([Q0, Q1, Q2, Q3, Q4, Q5, Q6, Q7]), "operationType" : NewBodyOperationType.ADD, "depth" : 9 * mm});
        }
    });
